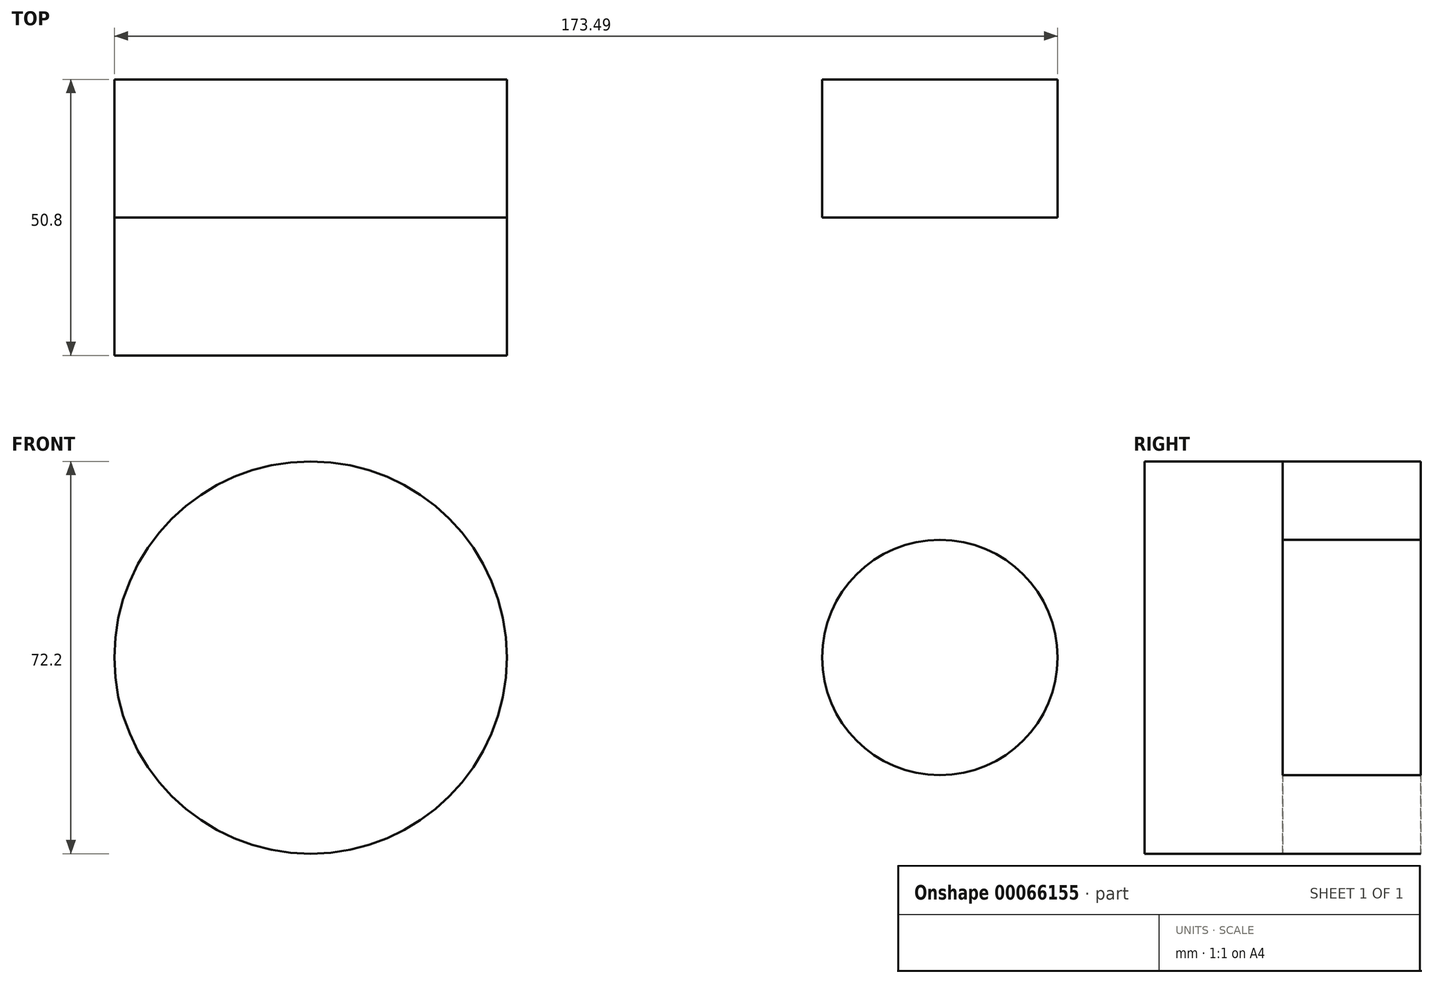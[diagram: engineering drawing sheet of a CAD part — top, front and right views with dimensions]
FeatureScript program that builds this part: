
annotation { "Feature Type Name" : "Feature", "Feature Type Description" : "" }
export const myFeature = defineFeature(function(context is Context, id is Id, definition is map)
    precondition{}
    {
        {
            var Q0;
            Q0=qCreatedBy(makeId("Front.planeOp"),FACE);
            var sketch = newSketch(context, id + "F0", { "sketchPlane" : qUnion([Q0])});
            skCircle(sketch, "E0", {"center": v(-55.64, 0) * mm, "radius": 36.1 * mm});
            skCircle(sketch, "E1", {"center": v(60.1, 0) * mm, "radius": 21.66 * mm});
            skLineSegment(sketch, "E2", {"start": v(-57.6, 36.04) * mm, "end": v(62.7, 21.5) * mm});
            skLineSegment(sketch, "E3", {"start": v(-52.2, -35.93) * mm, "end": v(62.7, -21.5) * mm});
            skSolve(sketch);
        }
        {
            var Q0;
            Q0 = qSketchRegion(id + "F0", true);
            extrude(context, id + "F1", {"entities" : qUnion([Q0]), "depth" : 25.4 * mm});
        }
        {
            var Q0;
            Q0 = qSketchRegion(id + "F0", true);
            var Q1;
            Q1=makeQuery(id+"F1.opExtrude","CAP_FACE",FACE,{"disambiguationData":[OSD([sQuery(id+"F0.wireOp",EDGE,"E0")])],"isStart":false});
            extrude(context, id + "F2", {"entities" : qUnion([Q0, Q1]), "depth" : 25.4 * mm});
        }
    });
